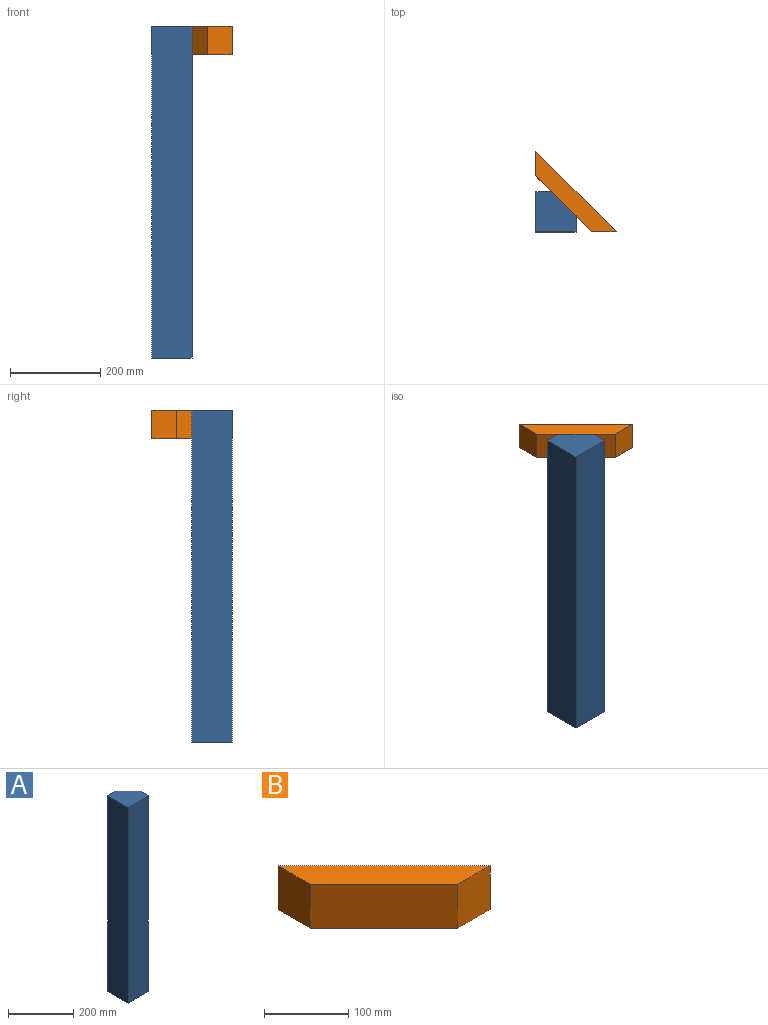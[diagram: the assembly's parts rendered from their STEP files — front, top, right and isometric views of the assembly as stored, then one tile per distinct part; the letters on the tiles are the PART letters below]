
ASSEMBLY  parts=2 mates=1
PART A: 8 faces, bbox 88.9x88.9x736.6 mm
  f0: plane 736.6x88.9mm, normal (1,0,0), area 62062.3mm2, adj f1,f3,f4,f5,f6,f7
  f1: plane 736.6x88.9mm, normal (0,1,0), area 62062.3mm2, adj f0,f2,f4,f5,f6,f7
  f2: plane 736.6x88.9mm, normal (-1,0,0), area 65483.7mm2, adj f1,f3,f4,f5
  f3: plane 736.6x88.9mm, normal (0,-1,0), area 65483.7mm2, adj f0,f2,f4,f5
  f4: plane 88.9x88.9mm, normal (0,0,-1), area 7903.2mm2, adj f0,f1,f2,f3
  f5: plane 88.9x88.9mm, normal (0,0,1), area 6451.6mm2, adj f0,f1,f2,f3,f6
  f6: plane 63.5x53.88mm, normal (0.71,0.71,0), area 4838.7mm2, adj f0,f1,f5,f7
  f7: plane 53.88x53.88mm, normal (0,0,1), area 1451.6mm2, adj f0,f1,f6
PART B: 6 faces, bbox 177.8x177.8x63.5 mm
  f0: plane 177.8x177.8mm, normal (0.71,0.71,0), area 15966.9mm2, adj f1,f3,f4,f5
  f1: plane 63.5x53.88mm, normal (-1,0,0), area 3421.5mm2, adj f0,f2,f4,f5
  f2: plane 123.92x123.92mm, normal (-0.71,-0.71,0), area 11128.2mm2, adj f1,f3,f4,f5
  f3: plane 63.5x53.88mm, normal (0,-1,0), area 3421.5mm2, adj f0,f2,f4,f5
  f4: plane 177.8x177.8mm, normal (0,0,-1), area 8128.5mm2, adj f0,f1,f2,f3
  f5: plane 177.8x177.8mm, normal (0,0,1), area 8128.5mm2, adj f0,f1,f2,f3
PLACE A t=(-19.22,-48.14,-145.65)mm
PLACE B t=(-19.22,-48.14,-145.65)mm
MATE fastened A.f6 <-> B.f2  axis (0.71,0.71,0) through (-81.18,-40.13,-177.4)mm
